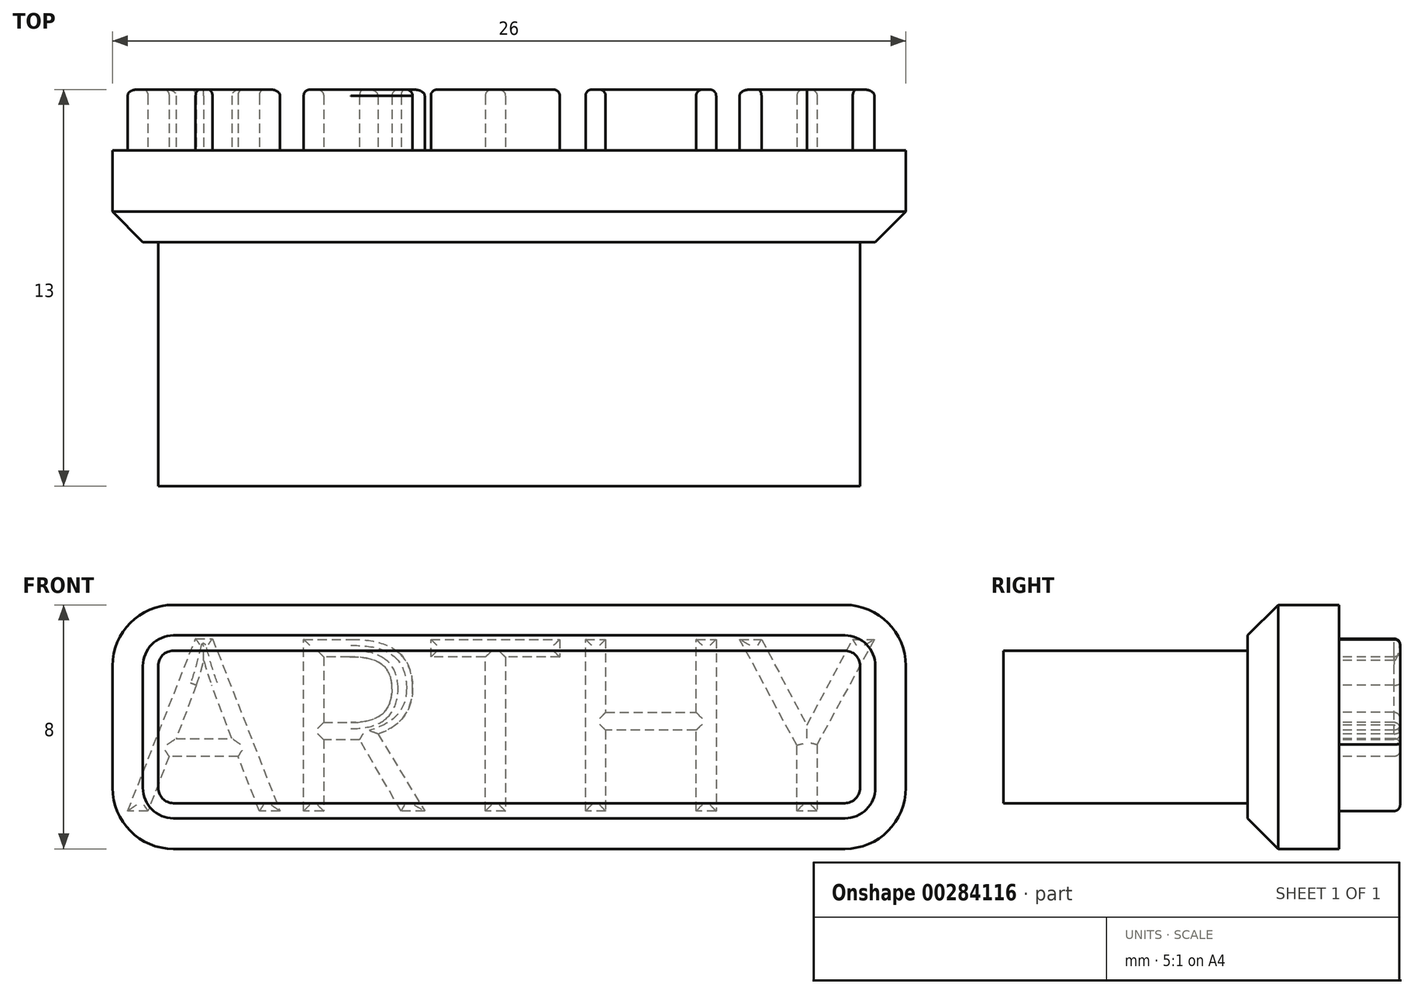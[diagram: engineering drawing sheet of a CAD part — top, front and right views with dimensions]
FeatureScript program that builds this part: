
annotation { "Feature Type Name" : "Feature", "Feature Type Description" : "" }
export const myFeature = defineFeature(function(context is Context, id is Id, definition is map)
    precondition{}
    {
        {
            var Q0;
            Q0=qCreatedBy(makeId("Front.planeOp"),FACE);
            var sketch = newSketch(context, id + "F0", { "sketchPlane" : qUnion([Q0])});
            skText(sketch, "E0", { "text": "ARTHY", "fontName": "OpenSans-Regular.ttf"});
            const initialGuessF0  = {"E0": [-0.0125, -0.00176, 1, 0, 0.00568]};
            skSetInitialGuess(sketch, initialGuessF0);
            skSolve(sketch);
        }
        {
            var Q0;
            Q0=qSketchRegion(id+"F0",true);
            extrude(context, id + "F1", {"entities" : qUnion([Q0]), "oppositeDirection" : true, "depth" : 2 * mm});
        }
        {
            var Q0;
            Q0=qCreatedBy(makeId("Front.planeOp"),FACE);
            var sketch = newSketch(context, id + "F2", { "sketchPlane" : qUnion([Q0])});
            skLineSegment(sketch, "E1.bottom", {"start": v(-13, 5) * mm, "end": v(13, 5) * mm});
            skLineSegment(sketch, "E1.top", {"start": v(-13, -3) * mm, "end": v(13, -3) * mm});
            skLineSegment(sketch, "E1.left", {"start": v(-13, 5) * mm, "end": v(-13, -3) * mm});
            skLineSegment(sketch, "E1.right", {"start": v(13, 5) * mm, "end": v(13, -3) * mm});
            skSolve(sketch);
        }
        {
            var Q0;
            Q0=qSketchRegion(id+"F2",true);
            extrude(context, id + "F3", {"entities" : qUnion([Q0]), "depth" : 3 * mm});
        }
        {
            var Q0;
            Q0=makeQuery(id+"F3.opExtrude","SWEPT_EDGE",EDGE,{"disambiguationData":[OSD([sQuery(id+"F2.wireOp",EDGE,"E1.top"),sQuery(id+"F2.wireOp",EDGE,"E1.left")])]});
            var Q1;
            Q1=makeQuery(id+"F3.opExtrude","SWEPT_EDGE",EDGE,{"disambiguationData":[OSD([sQuery(id+"F2.wireOp",EDGE,"E1.bottom"),sQuery(id+"F2.wireOp",EDGE,"E1.left")])]});
            var Q2;
            Q2=makeQuery(id+"F3.opExtrude","SWEPT_EDGE",EDGE,{"disambiguationData":[OSD([sQuery(id+"F2.wireOp",EDGE,"E1.top"),sQuery(id+"F2.wireOp",EDGE,"E1.right")])]});
            var Q3;
            Q3=makeQuery(id+"F3.opExtrude","SWEPT_EDGE",EDGE,{"disambiguationData":[OSD([sQuery(id+"F2.wireOp",EDGE,"E1.bottom"),sQuery(id+"F2.wireOp",EDGE,"E1.right")])]});
            fillet(context, id + "F4", {"entities" : qUnion([Q0, Q1, Q2, Q3]), "radius" : 2 * mm, "tangentPropagation" : true, "allowEdgeOverflow" : false});
        }
        {
            var Q0;
            Q0=makeQuery(id+"F3.opExtrude","CAP_FACE",FACE,{"disambiguationData":[OSD([sQuery(id+"F2.wireOp",EDGE,"E1.bottom"),sQuery(id+"F2.wireOp",EDGE,"E1.top"),sQuery(id+"F2.wireOp",EDGE,"E1.left"),sQuery(id+"F2.wireOp",EDGE,"E1.right")])],"isStart":false});
            chamfer(context, id + "F5", {"entities" : qUnion([Q0]), "width" : 1 * mm, "tangentPropagation" : true});
        }
        {
            var Q0;
            Q0=makeQuery(id+"F3.opExtrude","CAP_FACE",FACE,{"disambiguationData":[OSD([sQuery(id+"F2.wireOp",EDGE,"E1.bottom"),sQuery(id+"F2.wireOp",EDGE,"E1.top"),sQuery(id+"F2.wireOp",EDGE,"E1.left"),sQuery(id+"F2.wireOp",EDGE,"E1.right")])],"isStart":false});
            var sketch = newSketch(context, id + "F6", { "sketchPlane" : qUnion([Q0])});
            skArc(sketch, "E2.0", {"start": v(-11.5, -1) * mm, "mid": v(-11.35, -1.35) * mm, "end": v(-11, -1.5) * mm});
            skLineSegment(sketch, "E2.1", {"start": v(-11.5, 3) * mm, "end": v(-11.5, -1) * mm});
            skLineSegment(sketch, "E2.2", {"start": v(-11, -1.5) * mm, "end": v(11, -1.5) * mm});
            skArc(sketch, "E2.3", {"start": v(-11, 3.5) * mm, "mid": v(-11.35, 3.35) * mm, "end": v(-11.5, 3) * mm});
            skArc(sketch, "E2.4", {"start": v(11, -1.5) * mm, "mid": v(11.35, -1.35) * mm, "end": v(11.5, -1) * mm});
            skLineSegment(sketch, "E2.5", {"start": v(11.5, -1) * mm, "end": v(11.5, 3) * mm});
            skArc(sketch, "E2.6", {"start": v(11.5, 3) * mm, "mid": v(11.35, 3.35) * mm, "end": v(11, 3.5) * mm});
            skLineSegment(sketch, "E2.7", {"start": v(11, 3.5) * mm, "end": v(-11, 3.5) * mm});
            skSolve(sketch);
        }
        {
            var Q0;
            Q0 = qSketchRegion(id + "F6", true);
            extrude(context, id + "F7", {"entities" : qUnion([Q0]), "operationType" : NewBodyOperationType.ADD, "depth" : 8 * mm});
        }
        {
            var Q0;
            Q0=makeQuery(id+"F1.opExtrude","CAP_FACE",FACE,{"disambiguationData":[OSD([sQuery(id+"F0.wireOp",EDGE,"E0.sketch_text.stroke-51"),sQuery(id+"F0.wireOp",EDGE,"E0.sketch_text.stroke-52"),sQuery(id+"F0.wireOp",EDGE,"E0.sketch_text.stroke-53"),sQuery(id+"F0.wireOp",EDGE,"E0.sketch_text.stroke-54"),sQuery(id+"F0.wireOp",EDGE,"E0.sketch_text.stroke-55"),sQuery(id+"F0.wireOp",EDGE,"E0.sketch_text.stroke-56"),sQuery(id+"F0.wireOp",EDGE,"E0.sketch_text.stroke-57"),sQuery(id+"F0.wireOp",EDGE,"E0.sketch_text.stroke-58"),sQuery(id+"F0.wireOp",EDGE,"E0.sketch_text.stroke-59")])],"isStart":false});
            var Q1;
            Q1=makeQuery(id+"F1.opExtrude","CAP_FACE",FACE,{"disambiguationData":[OSD([sQuery(id+"F0.wireOp",EDGE,"E0.sketch_text.stroke-39"),sQuery(id+"F0.wireOp",EDGE,"E0.sketch_text.stroke-40"),sQuery(id+"F0.wireOp",EDGE,"E0.sketch_text.stroke-41"),sQuery(id+"F0.wireOp",EDGE,"E0.sketch_text.stroke-42"),sQuery(id+"F0.wireOp",EDGE,"E0.sketch_text.stroke-43"),sQuery(id+"F0.wireOp",EDGE,"E0.sketch_text.stroke-44"),sQuery(id+"F0.wireOp",EDGE,"E0.sketch_text.stroke-45"),sQuery(id+"F0.wireOp",EDGE,"E0.sketch_text.stroke-46"),sQuery(id+"F0.wireOp",EDGE,"E0.sketch_text.stroke-47"),sQuery(id+"F0.wireOp",EDGE,"E0.sketch_text.stroke-48"),sQuery(id+"F0.wireOp",EDGE,"E0.sketch_text.stroke-49"),sQuery(id+"F0.wireOp",EDGE,"E0.sketch_text.stroke-50")])],"isStart":false});
            var Q2;
            Q2=makeQuery(id+"F1.opExtrude","CAP_FACE",FACE,{"disambiguationData":[OSD([sQuery(id+"F0.wireOp",EDGE,"E0.sketch_text.stroke-31"),sQuery(id+"F0.wireOp",EDGE,"E0.sketch_text.stroke-32"),sQuery(id+"F0.wireOp",EDGE,"E0.sketch_text.stroke-33"),sQuery(id+"F0.wireOp",EDGE,"E0.sketch_text.stroke-34"),sQuery(id+"F0.wireOp",EDGE,"E0.sketch_text.stroke-35"),sQuery(id+"F0.wireOp",EDGE,"E0.sketch_text.stroke-36"),sQuery(id+"F0.wireOp",EDGE,"E0.sketch_text.stroke-37"),sQuery(id+"F0.wireOp",EDGE,"E0.sketch_text.stroke-38")])],"isStart":false});
            var Q3;
            Q3=makeQuery(id+"F1.opExtrude","CAP_FACE",FACE,{"disambiguationData":[OSD([sQuery(id+"F0.wireOp",EDGE,"E0.sketch_text.stroke-13"),sQuery(id+"F0.wireOp",EDGE,"E0.sketch_text.stroke-14"),sQuery(id+"F0.wireOp",EDGE,"E0.sketch_text.stroke-15"),sQuery(id+"F0.wireOp",EDGE,"E0.sketch_text.stroke-16"),sQuery(id+"F0.wireOp",EDGE,"E0.sketch_text.stroke-17"),sQuery(id+"F0.wireOp",EDGE,"E0.sketch_text.stroke-18"),sQuery(id+"F0.wireOp",EDGE,"E0.sketch_text.stroke-19"),sQuery(id+"F0.wireOp",EDGE,"E0.sketch_text.stroke-20"),sQuery(id+"F0.wireOp",EDGE,"E0.sketch_text.stroke-21"),sQuery(id+"F0.wireOp",EDGE,"E0.sketch_text.stroke-22"),sQuery(id+"F0.wireOp",EDGE,"E0.sketch_text.stroke-23"),sQuery(id+"F0.wireOp",EDGE,"E0.sketch_text.stroke-24"),sQuery(id+"F0.wireOp",EDGE,"E0.sketch_text.stroke-25"),sQuery(id+"F0.wireOp",EDGE,"E0.sketch_text.stroke-26"),sQuery(id+"F0.wireOp",EDGE,"E0.sketch_text.stroke-27"),sQuery(id+"F0.wireOp",EDGE,"E0.sketch_text.stroke-28"),sQuery(id+"F0.wireOp",EDGE,"E0.sketch_text.stroke-29"),sQuery(id+"F0.wireOp",EDGE,"E0.sketch_text.stroke-30")])],"isStart":false});
            var Q4;
            Q4=makeQuery(id+"F1.opExtrude","CAP_FACE",FACE,{"disambiguationData":[OSD([sQuery(id+"F0.wireOp",EDGE,"E0.sketch_text.stroke-0"),sQuery(id+"F0.wireOp",EDGE,"E0.sketch_text.stroke-1"),sQuery(id+"F0.wireOp",EDGE,"E0.sketch_text.stroke-2"),sQuery(id+"F0.wireOp",EDGE,"E0.sketch_text.stroke-3"),sQuery(id+"F0.wireOp",EDGE,"E0.sketch_text.stroke-4"),sQuery(id+"F0.wireOp",EDGE,"E0.sketch_text.stroke-5"),sQuery(id+"F0.wireOp",EDGE,"E0.sketch_text.stroke-6"),sQuery(id+"F0.wireOp",EDGE,"E0.sketch_text.stroke-7"),sQuery(id+"F0.wireOp",EDGE,"E0.sketch_text.stroke-8"),sQuery(id+"F0.wireOp",EDGE,"E0.sketch_text.stroke-9"),sQuery(id+"F0.wireOp",EDGE,"E0.sketch_text.stroke-10"),sQuery(id+"F0.wireOp",EDGE,"E0.sketch_text.stroke-11"),sQuery(id+"F0.wireOp",EDGE,"E0.sketch_text.stroke-12")])],"isStart":false});
            fillet(context, id + "F8", {"entities" : qUnion([Q0, Q1, Q2, Q3, Q4]), "radius" : 0.2 * mm, "tangentPropagation" : true, "allowEdgeOverflow" : false});
        }
    });
